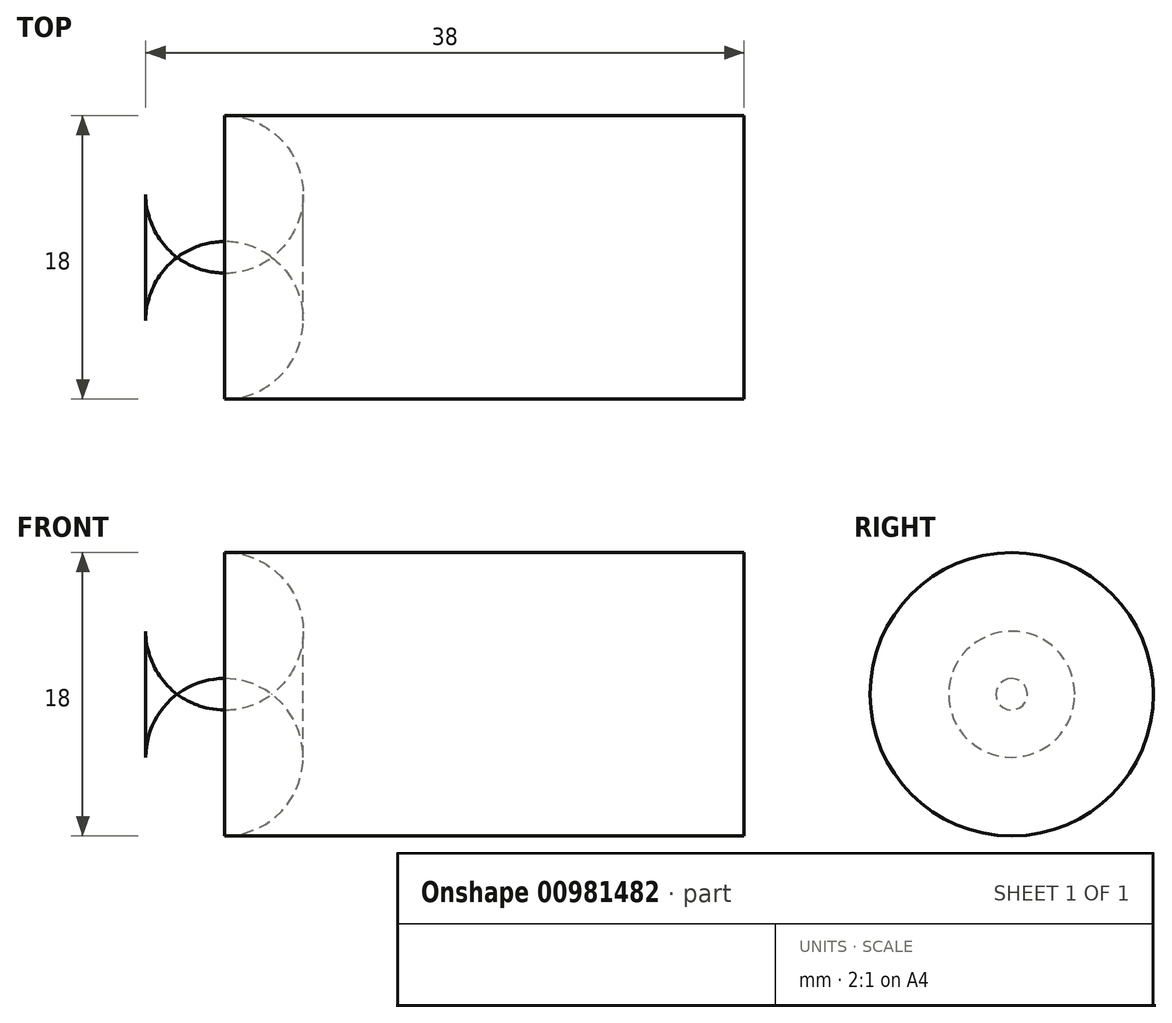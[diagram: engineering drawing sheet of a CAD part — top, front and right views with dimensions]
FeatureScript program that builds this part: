
annotation { "Feature Type Name" : "Feature", "Feature Type Description" : "" }
export const myFeature = defineFeature(function(context is Context, id is Id, definition is map)
    precondition{}
    {
        {
            var Q0;
            Q0=qCreatedBy(makeId("Right.planeOp"),FACE);
            var sketch = newSketch(context, id + "F0", { "sketchPlane" : qUnion([Q0])});
            skCircle(sketch, "E0", {"center": v(0, 0) * mm, "radius": 9 * mm});
            skSolve(sketch);
        }
        {
            var Q0;
            Q0=makeQuery(id+"F0.imprint","IMPRINT",FACE,{"disambiguationData":[TD([[makeQuery(id+"F0.imprint","IMPRINT",EDGE,{"derivedFrom":sQuery(id+"F0.wireOp",EDGE,"E0")}),1.0]])]});
            extrude(context, id + "F1", {"entities" : qUnion([Q0]), "oppositeDirection" : true, "depth" : 38 * mm, "offsetDistance" : 25 * mm});
        }
        {
            var Q0;
            Q0=makeQuery(id+"F1.opExtrude","CAP_EDGE",EDGE,{"disambiguationData":[OSD([sQuery(id+"F0.wireOp",EDGE,"E0")])],"isStart":false});
            fillet(context, id + "F2", {"entities" : qUnion([Q0]), "radius" : 5 * mm, "tangentPropagation" : true, "allowEdgeOverflow" : false});
        }
    });
